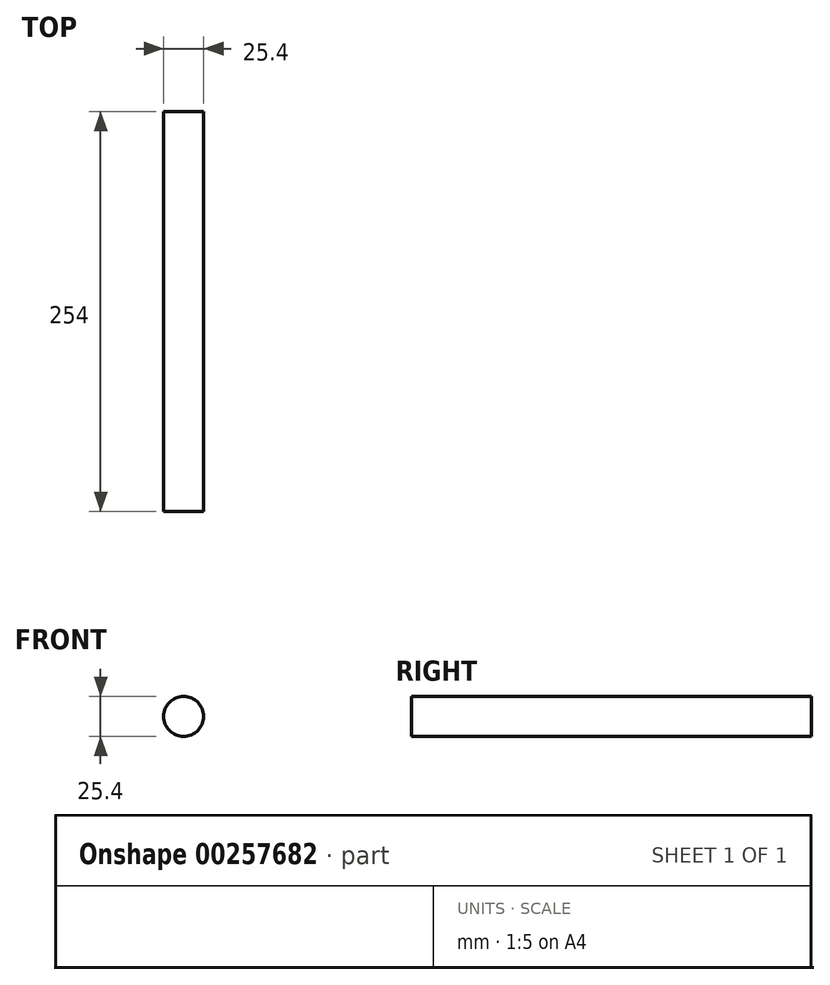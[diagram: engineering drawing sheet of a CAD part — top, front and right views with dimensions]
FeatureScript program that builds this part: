
annotation { "Feature Type Name" : "Feature", "Feature Type Description" : "" }
export const myFeature = defineFeature(function(context is Context, id is Id, definition is map)
    precondition{}
    {
        {
            var Q0;
            Q0=qCreatedBy(makeId("Front.planeOp"),FACE);
            var sketch = newSketch(context, id + "F0", { "sketchPlane" : qUnion([Q0])});
            skCircle(sketch, "E0", {"center": v(0, 0) * mm, "radius": 12.7 * mm});
            skSolve(sketch);
        }
        {
            var Q0;
            Q0=makeQuery(id+"F0.imprint","IMPRINT",FACE,{"disambiguationData":[TD([[makeQuery(id+"F0.imprint","IMPRINT",EDGE,{"derivedFrom":sQuery(id+"F0.wireOp",EDGE,"E0")}),1.0]])]});
            extrude(context, id + "F1", {"entities" : qUnion([Q0]), "depth" : 254 * mm});
        }
    });
